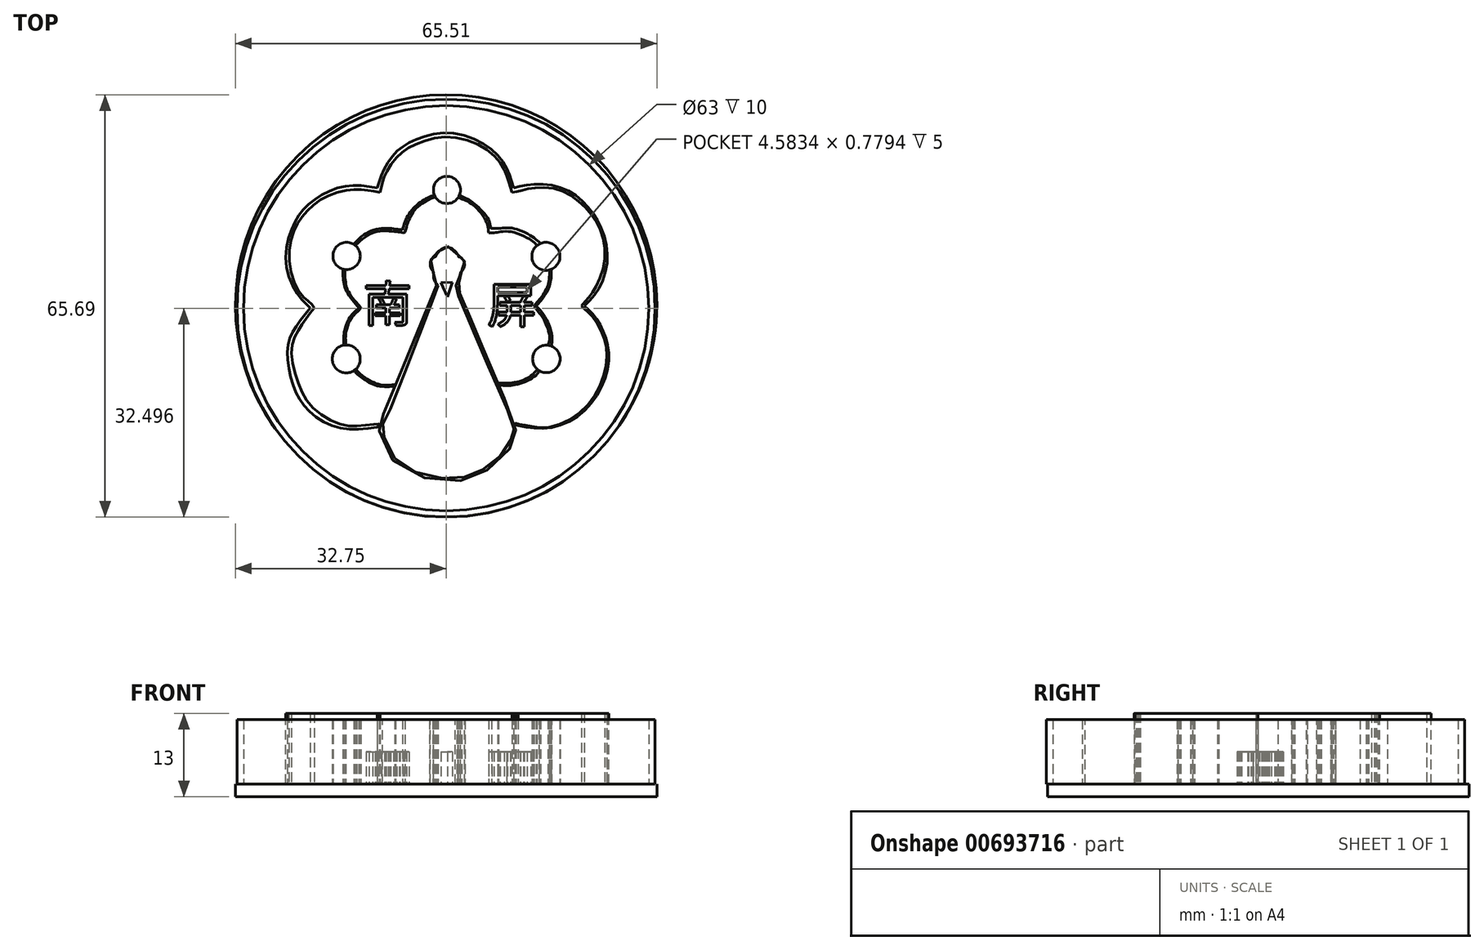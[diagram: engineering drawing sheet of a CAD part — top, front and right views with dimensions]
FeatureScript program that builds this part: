
annotation { "Feature Type Name" : "Feature", "Feature Type Description" : "" }
export const myFeature = defineFeature(function(context is Context, id is Id, definition is map)
    precondition{}
    {
        {
            var Q0;
            Q0=qCreatedBy(makeId("Top.planeOp"),FACE);
            var sketch = newSketch(context, id + "F0", { "sketchPlane" : qUnion([Q0])});
            skCircle(sketch, "E0", {"center": v(0, -1.24) * mm, "radius": 32.5 * mm});
            skCircle(sketch, "E1", {"center": v(0, -1.24) * mm, "radius": 31.5 * mm});
            skSolve(sketch);
        }
        {
            var Q0;
            Q0 = qSketchRegion(id + "F0", true);
            extrude(context, id + "F1", {"entities" : qUnion([Q0]), "depth" : 10 * mm, "offsetDistance" : 25 * mm});
        }
        {
            var Q0;
            Q0=qCreatedBy(makeId("Top.planeOp"),FACE);
            var sketch = newSketch(context, id + "F2", { "sketchPlane" : qUnion([Q0])});
            skCircle(sketch, "E2", {"center": v(15.51, 6.81) * mm, "radius": 2.18 * mm});
            skCircle(sketch, "E3", {"center": v(15.58, -9.13) * mm, "radius": 2.14 * mm});
            skCircle(sketch, "E4", {"center": v(-15.52, -9.14) * mm, "radius": 2.18 * mm});
            skCircle(sketch, "E5", {"center": v(-15.47, 6.87) * mm, "radius": 2.12 * mm});
            skCircle(sketch, "E6", {"center": v(0.13, 17.14) * mm, "radius": 2.1 * mm});
            skSolve(sketch);
        }
        {
            var Q0;
            Q0 = qSketchRegion(id + "F2", true);
            extrude(context, id + "F3", {"entities" : qUnion([Q0]), "depth" : 10 * mm, "offsetDistance" : 25 * mm});
        }
        {
            var Q0;
            Q0=qCreatedBy(makeId("Top.planeOp"),FACE);
            var sketch = newSketch(context, id + "F4", { "sketchPlane" : qUnion([Q0])});
            skFitSpline(sketch, "E7", {"points": [v(-21.1, -1.21) * mm, v(-22.88, 0.65) * mm, v(-24.9, 5.56) * mm, v(-23.94, 11.21) * mm, v(-22.06, 14.24) * mm, v(-18.83, 16.65) * mm, v(-14.76, 17.84) * mm, v(-10.69, 17.46) * mm], "startDerivative": vector(-15.64, 13.84) * mm, "endDerivative": vector(28.64, -5.04) * mm});
            skFitSpline(sketch, "E8", {"points": [v(-10.69, 17.46) * mm, v(-9.79, 20.1) * mm, v(-7.74, 23.04) * mm, v(-4.88, 24.89) * mm, v(0.49, 26.01) * mm, v(6.8, 23.66) * mm, v(9.52, 20.32) * mm, v(10.5, 17.46) * mm], "startDerivative": vector(5.97, 21.97) * mm, "endDerivative": vector(6.22, -23.18) * mm});
            skFitSpline(sketch, "E9", {"points": [v(10.5, 17.46) * mm, v(13.42, 18.02) * mm, v(18, 17.46) * mm, v(21.7, 14.88) * mm, v(24.05, 11.4) * mm, v(25.07, 6.52) * mm, v(23.76, 1.87) * mm, v(21.5, -0.88) * mm], "startDerivative": vector(22.64, 5.92) * mm, "endDerivative": vector(-18.53, -18.75) * mm});
            skFitSpline(sketch, "E10", {"points": [v(21.5, -0.88) * mm, v(23.02, -2.42) * mm, v(24.53, -5.1) * mm, v(25.3, -8.5) * mm, v(24.21, -13.35) * mm, v(20.62, -17.91) * mm, v(15.57, -19.91) * mm, v(11.2, -19.5) * mm], "startDerivative": vector(15.05, -13.26) * mm, "endDerivative": vector(-28.75, 5.7) * mm});
            skFitSpline(sketch, "E11", {"points": [v(-21.1, -1.21) * mm, v(-23.65, -4.6) * mm, v(-24.66, -7.87) * mm, v(-23.85, -12.93) * mm, v(-21.72, -16.82) * mm, v(-16.96, -19.78) * mm, v(-10.69, -19.78) * mm], "startDerivative": vector(-18.06, -21.75) * mm, "endDerivative": vector(33.82, 4.07) * mm});
            skFitSpline(sketch, "E12", {"points": [v(-10.69, -19.78) * mm, v(-10.52, -19.78) * mm, v(-10.39, -19.27) * mm, v(-10.5, -19.22) * mm, v(-12.99, -19.5) * mm, v(-16.5, -19.27) * mm, v(-20.9, -16.53) * mm, v(-23.06, -12.64) * mm, v(-24.05, -7.85) * mm, v(-23.13, -4.96) * mm, v(-21.74, -2.85) * mm, v(-20.5, -1.21) * mm], "startDerivative": vector(6.87, -2.87) * mm, "endDerivative": vector(13.9, 18.09) * mm});
            skFitSpline(sketch, "E13", {"points": [v(-20.5, -1.21) * mm, v(-21.1, -0.42) * mm, v(-22.5, 0.83) * mm, v(-24.36, 5.7) * mm, v(-23.6, 10.88) * mm, v(-21.7, 13.76) * mm, v(-18.68, 16.06) * mm, v(-14.7, 17.18) * mm, v(-12.24, 17.1) * mm, v(-10.28, 16.76) * mm], "startDerivative": vector(-8, 12.9) * mm, "endDerivative": vector(21.6, -4.05) * mm});
            skFitSpline(sketch, "E14", {"points": [v(-10.28, 16.76) * mm, v(-9.96, 18.1) * mm, v(-9.35, 19.75) * mm, v(-7.43, 22.48) * mm, v(-4.73, 24.25) * mm, v(0.43, 25.39) * mm, v(6.35, 23.4) * mm, v(9.03, 20.32) * mm, v(9.75, 18.32) * mm, v(10.22, 16.76) * mm], "startDerivative": vector(4.05, 17.8) * mm, "endDerivative": vector(5.84, -18.76) * mm});
            skFitSpline(sketch, "E15", {"points": [v(10.22, 16.76) * mm, v(11.53, 17.03) * mm, v(13.59, 17.46) * mm, v(17.82, 17.1) * mm, v(21.5, 14.55) * mm, v(23.76, 11.38) * mm, v(24.66, 6.7) * mm, v(23.34, 2.15) * mm, v(22.05, 0.32) * mm, v(21.06, -0.88) * mm], "startDerivative": vector(17.5, 3.26) * mm, "endDerivative": vector(-12.22, -15.06) * mm});
            skFitSpline(sketch, "E16", {"points": [v(21.06, -0.88) * mm, v(21.72, -1.57) * mm, v(22.75, -2.52) * mm, v(24.3, -5.23) * mm, v(25, -8.52) * mm, v(24, -13.1) * mm, v(20.64, -17.6) * mm, v(15.57, -19.78) * mm, v(12.62, -19.51) * mm, v(11.2, -19.26) * mm, v(10.7, -19.16) * mm, v(10.82, -19.44) * mm], "startDerivative": vector(10.7, -12.03) * mm, "endDerivative": vector(6.4, -11.24) * mm});
            skFitSpline(sketch, "E17", {"points": [v(10.82, -19.44) * mm, v(11.2, -19.5) * mm], "startDerivative": vector(0.4, -0.06) * mm, "endDerivative": vector(0.4, -0.06) * mm});
            skSolve(sketch);
        }
        {
            var Q0;
            Q0 = qSketchRegion(id + "F4", true);
            extrude(context, id + "F5", {"entities" : qUnion([Q0]), "depth" : 5 * mm, "offsetDistance" : 25 * mm});
        }
        {
            var Q0;
            Q0=qCreatedBy(makeId("Top.planeOp"),FACE);
            var sketch = newSketch(context, id + "F6", { "sketchPlane" : qUnion([Q0])});
            skSolve(sketch);
        }
        {
            var Q0;
            Q0=qCreatedBy(makeId("Top.planeOp"),FACE);
            var sketch = newSketch(context, id + "F7", { "sketchPlane" : qUnion([Q0])});
            skCircle(sketch, "E18", {"center": v(0, -0.8) * mm, "radius": 32.75 * mm});
            skPoint(sketch, "E18.first.point", {"position": v(31.84, -8.48) * mm});
            skPoint(sketch, "E18.second.point", {"position": v(-32.05, 5.96) * mm});
            skPoint(sketch, "E18.third.point", {"position": v(-26.8, -19.64) * mm});
            skSolve(sketch);
        }
        {
            var Q0;
            Q0 = qSketchRegion(id + "F7", true);
            extrude(context, id + "F8", {"entities" : qUnion([Q0]), "oppositeDirection" : true, "depth" : 2 * mm, "offsetDistance" : 25 * mm});
        }
        {
            var Q0;
            Q0 = qSketchRegion(id + "F6", true);
            var Q1;
            Q1=makeQuery(id+"F5.opExtrude","CAP_FACE",FACE,{"disambiguationData":[OSD([sQuery(id+"F4.wireOp",EDGE,"E7"),sQuery(id+"F4.wireOp",EDGE,"E8"),sQuery(id+"F4.wireOp",EDGE,"E9"),sQuery(id+"F4.wireOp",EDGE,"E10"),sQuery(id+"F4.wireOp",EDGE,"E11"),sQuery(id+"F4.wireOp",EDGE,"E12"),sQuery(id+"F4.wireOp",EDGE,"E13"),sQuery(id+"F4.wireOp",EDGE,"E14"),sQuery(id+"F4.wireOp",EDGE,"E15"),sQuery(id+"F4.wireOp",EDGE,"E16"),sQuery(id+"F4.wireOp",EDGE,"E17")])],"isStart":false});
            extrude(context, id + "F9", {"entities" : qUnion([Q0, Q1]), "operationType" : NewBodyOperationType.ADD, "depth" : 6 * mm, "offsetDistance" : 25 * mm});
        }
        {
            var Q0;
            Q0=qCreatedBy(makeId("Top.planeOp"),FACE);
            var sketch = newSketch(context, id + "F10", { "sketchPlane" : qUnion([Q0])});
            skFitSpline(sketch, "E19", {"points": [v(-1.5, 2.26) * mm, v(-2.02, 3.37) * mm, v(-2, 4.39) * mm, v(-2.02, 4.38) * mm, v(-2.45, 5.02) * mm, v(-2.53, 5.85) * mm, v(-2.3, 6.4) * mm, v(-1.75, 6.8) * mm, v(-1.71, 6.8) * mm, v(-1.58, 7.1) * mm, v(-0.85, 7.94) * mm, v(-0.37, 8.25) * mm, v(0.05, 8.36) * mm, v(0.5, 8.31) * mm, v(1.26, 7.92) * mm, v(1.9, 7.1) * mm, v(1.97, 6.81) * mm, v(1.97, 6.79) * mm, v(2.07, 6.8) * mm, v(2.47, 6.61) * mm, v(2.84, 6.07) * mm, v(2.94, 5.37) * mm, v(2.66, 4.61) * mm, v(2.4, 4.4) * mm, v(2.35, 4.38) * mm, v(2.4, 4.3) * mm, v(2.28, 3.57) * mm, v(2.07, 2.85) * mm, v(1.76, 2.2) * mm, v(1.7, 2.1) * mm, v(1.7, 2.08) * mm, v(1.92, 1.53) * mm, v(3.06, -1.03) * mm, v(4.18, -3.76) * mm, v(7.4, -11.4) * mm, v(10.83, -19.9) * mm, v(10.8, -20.4) * mm, v(10.5, -21.78) * mm, v(8.69, -24.67) * mm, v(5, -27.13) * mm, v(1.71, -28.1) * mm, v(-4.27, -27.38) * mm, v(-8.87, -24.14) * mm, v(-10.4, -20.11) * mm, v(-10.3, -19.12) * mm, v(-9.65, -17.5) * mm, v(-3.8, -3.3) * mm, v(-1.57, 1.92) * mm, v(-1.5, 2.26) * mm]});
            skFitSpline(sketch, "E20", {"points": [v(-1.25, 2.25) * mm, v(-1.39, 1.81) * mm, v(-3.47, -3.55) * mm, v(-9.04, -17.75) * mm, v(-9.8, -19.26) * mm, v(-9.88, -20.11) * mm, v(-8.6, -23.75) * mm, v(-4.24, -26.95) * mm, v(1.7, -27.72) * mm, v(4.78, -26.84) * mm, v(8.23, -24.49) * mm, v(10.09, -21.67) * mm, v(10.47, -20.33) * mm, v(10.53, -19.9) * mm, v(8.7, -15.16) * mm, v(7.1, -11.5) * mm, v(3.84, -3.85) * mm, v(2.71, -1.2) * mm, v(1.44, 2.02) * mm, v(1.46, 2.1) * mm, v(1.57, 2.35) * mm, v(1.92, 3.04) * mm, v(2.11, 3.7) * mm, v(2.26, 4.21) * mm, v(2.24, 4.28) * mm, v(2.23, 4.34) * mm, v(2.28, 4.38) * mm], "startDerivative": vector(-5.5, -19.67) * mm, "endDerivative": vector(9.01, 2.13) * mm});
            skFitSpline(sketch, "E21", {"points": [v(2.28, 4.38) * mm, v(2.3, 4.42) * mm, v(2.48, 4.5) * mm, v(2.58, 4.65) * mm, v(2.72, 4.89) * mm, v(2.88, 5.37) * mm, v(2.78, 6.05) * mm, v(2.45, 6.56) * mm, v(2.09, 6.73) * mm, v(1.94, 6.7) * mm, v(1.92, 6.71) * mm, v(1.9, 6.7) * mm, v(1.91, 6.81) * mm, v(1.85, 7.06) * mm, v(1.2, 7.85) * mm, v(0.48, 8.23) * mm, v(0.07, 8.27) * mm, v(-0.34, 8.16) * mm, v(-0.77, 7.9) * mm, v(-1.5, 7.07) * mm, v(-1.66, 6.76) * mm, v(-1.67, 6.75) * mm, v(-1.74, 6.74) * mm, v(-2.26, 6.37) * mm, v(-2.46, 5.84) * mm, v(-2.48, 5.38) * mm, v(-2.4, 5.06) * mm, v(-2.08, 4.5) * mm, v(-1.97, 4.43) * mm, v(-1.97, 4.44) * mm, v(-1.96, 4.24) * mm, v(-1.95, 3.57) * mm, v(-1.81, 3.02) * mm, v(-1.25, 2.25) * mm], "startDerivative": vector(0.63, 3.84) * mm, "endDerivative": vector(12.96, -15.51) * mm});
            skSolve(sketch);
        }
        {
            var Q0;
            Q0 = qSketchRegion(id + "F10", true);
            extrude(context, id + "F11", {"entities" : qUnion([Q0]), "operationType" : NewBodyOperationType.ADD, "depth" : 10 * mm, "offsetDistance" : 25 * mm});
        }
        {
            var Q0;
            Q0=qCreatedBy(makeId("Top.planeOp"),FACE);
            var sketch = newSketch(context, id + "F12", { "sketchPlane" : qUnion([Q0])});
            skFitSpline(sketch, "E22", {"points": [v(-1.83, 16.35) * mm, v(-3.1, 15.82) * mm, v(-4.84, 14.55) * mm, v(-6.14, 12.76) * mm, v(-6.8, 10.9) * mm], "startDerivative": vector(-5.76, -2.1) * mm, "endDerivative": vector(-2.16, -7.38) * mm});
            skFitSpline(sketch, "E23", {"points": [v(-6.8, 10.9) * mm, v(-7.69, 11.05) * mm, v(-9.21, 11.2) * mm, v(-11.34, 10.9) * mm, v(-13.43, 9.67) * mm, v(-14.32, 8.7) * mm], "startDerivative": vector(-5.58, 0.95) * mm, "endDerivative": vector(-4.17, -5.18) * mm});
            skFitSpline(sketch, "E24", {"points": [v(-14.32, 8.7) * mm, v(-14.14, 8.57) * mm], "startDerivative": vector(0.18, -0.14) * mm, "endDerivative": vector(0.18, -0.14) * mm});
            skFitSpline(sketch, "E25", {"points": [v(-14.14, 8.57) * mm, v(-13.93, 8.7) * mm, v(-13.22, 9.35) * mm, v(-11.23, 10.55) * mm, v(-9.18, 10.77) * mm, v(-7.72, 10.66) * mm, v(-7.08, 10.55) * mm, v(-6.55, 10.48) * mm, v(-6.37, 10.62) * mm], "startDerivative": vector(2.96, 1.72) * mm, "endDerivative": vector(2.27, 2.91) * mm});
            skFitSpline(sketch, "E26", {"points": [v(-6.37, 10.62) * mm, v(-5.7, 12.63) * mm, v(-4.63, 14.3) * mm, v(-2.92, 15.52) * mm, v(-2.14, 15.9) * mm, v(-1.7, 16.07) * mm], "startDerivative": vector(2.46, 8.41) * mm, "endDerivative": vector(3.68, 1.34) * mm});
            skFitSpline(sketch, "E27", {"points": [v(-1.7, 16.07) * mm, v(-1.83, 16.35) * mm], "startDerivative": vector(-0.13, 0.28) * mm, "endDerivative": vector(-0.13, 0.28) * mm});
            skFitSpline(sketch, "E28", {"points": [v(-15.98, 4.82) * mm, v(-16.04, 4.32) * mm, v(-15.9, 2.65) * mm, v(-15.24, 0.96) * mm, v(-13.69, -1.04) * mm, v(-13.57, -1.2) * mm, v(-13.57, -1.17) * mm], "startDerivative": vector(-0.58, -3.26) * mm, "endDerivative": vector(-0.13, 1.48) * mm});
            skFitSpline(sketch, "E29", {"points": [v(-13.57, -1.2) * mm, v(-14.25, -1.8) * mm, v(-15.1, -2.9) * mm, v(-15.88, -5.28) * mm, v(-15.88, -6.97) * mm], "startDerivative": vector(-3.52, -3) * mm, "endDerivative": vector(0.54, -6.05) * mm});
            skFitSpline(sketch, "E30", {"points": [v(-15.88, -6.97) * mm, v(-15.87, -7) * mm], "startDerivative": vector(0, -0.03) * mm, "endDerivative": vector(0, -0.03) * mm});
            skFitSpline(sketch, "E31", {"points": [v(-15.87, -7) * mm, v(-15.6, -6.97) * mm], "startDerivative": vector(0.27, 0.03) * mm, "endDerivative": vector(0.27, 0.03) * mm});
            skFitSpline(sketch, "E32", {"points": [v(-15.6, -6.97) * mm, v(-15.6, -6.48) * mm, v(-15.6, -5.4) * mm, v(-14.85, -3) * mm, v(-14, -1.99) * mm, v(-13.57, -1.58) * mm, v(-13.25, -1.2) * mm, v(-13.22, -1.2) * mm], "startDerivative": vector(0.1, 4) * mm, "endDerivative": vector(0.71, -0.32) * mm});
            skFitSpline(sketch, "E33", {"points": [v(-13.22, -1.2) * mm, v(-13.4, -1) * mm, v(-15, 0.99) * mm, v(-15.6, 2.65) * mm, v(-15.73, 4.3) * mm, v(-15.68, 4.76) * mm], "startDerivative": vector(-1.15, 1.57) * mm, "endDerivative": vector(0.61, 3.02) * mm});
            skFitSpline(sketch, "E34", {"points": [v(-15.98, 4.82) * mm, v(-15.68, 4.76) * mm], "startDerivative": vector(0.3, -0.06) * mm, "endDerivative": vector(0.3, -0.06) * mm});
            skFitSpline(sketch, "E35", {"points": [v(-14.26, -10.9) * mm, v(-12.72, -12.4) * mm, v(-10.42, -13.4) * mm, v(-8, -13.46) * mm], "startDerivative": vector(4.4, -4.96) * mm, "endDerivative": vector(7.17, 0.46) * mm});
            skFitSpline(sketch, "E36", {"points": [v(-8, -13.46) * mm, v(-7.85, -13.1) * mm, v(-7.88, -13.1) * mm], "startDerivative": vector(0.32, 0.65) * mm, "endDerivative": vector(-0.19, -0.08) * mm});
            skFitSpline(sketch, "E37", {"points": [v(-7.87, -13.1) * mm, v(-8.75, -13.1) * mm, v(-10.32, -13.02) * mm, v(-12.44, -12.16) * mm, v(-13.5, -11.33) * mm, v(-14.03, -10.72) * mm], "startDerivative": vector(-5.06, 0.07) * mm, "endDerivative": vector(-3.17, 3.86) * mm});
            skFitSpline(sketch, "E38", {"points": [v(-14.03, -10.72) * mm, v(-14.26, -10.9) * mm], "startDerivative": vector(-0.23, -0.18) * mm, "endDerivative": vector(-0.23, -0.18) * mm});
            skFitSpline(sketch, "E39", {"points": [v(8.18, -13.17) * mm, v(8.75, -13.23) * mm, v(9.97, -13.25) * mm, v(12.33, -12.67) * mm, v(14.3, -11.33) * mm, v(14.5, -10.98) * mm, v(14.5, -11) * mm], "startDerivative": vector(3.96, -0.53) * mm, "endDerivative": vector(-0.08, -0.8) * mm});
            skFitSpline(sketch, "E40", {"points": [v(14.51, -10.99) * mm, v(14.14, -10.72) * mm], "startDerivative": vector(-0.37, 0.27) * mm, "endDerivative": vector(-0.37, 0.27) * mm});
            skFitSpline(sketch, "E41", {"points": [v(14.14, -10.72) * mm, v(13.93, -11.08) * mm, v(12.29, -12.3) * mm, v(10, -12.87) * mm, v(8.75, -12.92) * mm, v(8.05, -12.87) * mm], "startDerivative": vector(-1.14, -2.73) * mm, "endDerivative": vector(-4.4, 0.35) * mm});
            skFitSpline(sketch, "E42", {"points": [v(8.05, -12.87) * mm, v(8.18, -13.17) * mm], "startDerivative": vector(0.13, -0.3) * mm, "endDerivative": vector(0.13, -0.3) * mm});
            skFitSpline(sketch, "E43", {"points": [v(2.04, 16.35) * mm, v(3.2, 15.82) * mm, v(4.82, 14.64) * mm, v(6.68, 12.32) * mm, v(6.99, 11.2) * mm, v(7.06, 11.2) * mm], "startDerivative": vector(5.68, -2.36) * mm, "endDerivative": vector(1.66, 0.6) * mm});
            skFitSpline(sketch, "E44", {"points": [v(7.06, 11.2) * mm, v(8.35, 11.2) * mm, v(10.34, 11.2) * mm, v(13.15, 10.04) * mm, v(14.67, 8.85) * mm], "startDerivative": vector(6.18, -0.2) * mm, "endDerivative": vector(5.46, -4.87) * mm});
            skFitSpline(sketch, "E45", {"points": [v(14.67, 8.85) * mm, v(14.14, 8.5) * mm], "startDerivative": vector(-0.52, -0.35) * mm, "endDerivative": vector(-0.52, -0.35) * mm});
            skFitSpline(sketch, "E46", {"points": [v(14.14, 8.5) * mm, v(13.81, 8.85) * mm, v(12.96, 9.5) * mm, v(10.2, 10.62) * mm, v(8.35, 10.62) * mm, v(7.5, 10.49) * mm, v(6.61, 10.49) * mm], "startDerivative": vector(-2.93, 3.27) * mm, "endDerivative": vector(-6.47, 0.26) * mm});
            skFitSpline(sketch, "E47", {"points": [v(6.61, 10.49) * mm, v(6.3, 12.08) * mm, v(4.7, 14.35) * mm, v(3.14, 15.45) * mm, v(2.25, 15.82) * mm, v(1.9, 15.96) * mm], "startDerivative": vector(-0.58, 7.07) * mm, "endDerivative": vector(-3.02, 1.32) * mm});
            skFitSpline(sketch, "E48", {"points": [v(1.9, 15.96) * mm, v(2.04, 16.35) * mm], "startDerivative": vector(0.14, 0.4) * mm, "endDerivative": vector(0.14, 0.4) * mm});
            skFitSpline(sketch, "E49", {"points": [v(16.3, 4.76) * mm, v(16.34, 4.4) * mm, v(16.27, 3.1) * mm, v(15.83, 1.6) * mm, v(14.94, 0.19) * mm, v(14, -0.93) * mm], "startDerivative": vector(0.42, -2.76) * mm, "endDerivative": vector(-4.24, -4.87) * mm});
            skFitSpline(sketch, "E50", {"points": [v(14, -0.93) * mm, v(14.3, -1.2) * mm, v(15.02, -2.06) * mm, v(15.45, -2.7) * mm, v(16.04, -3.98) * mm, v(16.48, -5.75) * mm, v(16.34, -7.13) * mm], "startDerivative": vector(2.54, -2.2) * mm, "endDerivative": vector(-1.38, -7.07) * mm});
            skFitSpline(sketch, "E51", {"points": [v(16.34, -7.13) * mm, v(15.82, -7) * mm], "startDerivative": vector(-0.52, 0.14) * mm, "endDerivative": vector(-0.52, 0.14) * mm});
            skFitSpline(sketch, "E52", {"points": [v(15.82, -7) * mm, v(16, -6.6) * mm, v(16.11, -5.78) * mm, v(15.67, -4.1) * mm, v(15.13, -2.9) * mm, v(14.8, -2.39) * mm, v(14, -1.4) * mm, v(13.65, -1) * mm], "startDerivative": vector(1.84, 3.7) * mm, "endDerivative": vector(-2.8, 3.1) * mm});
            skFitSpline(sketch, "E53", {"points": [v(13.65, -1) * mm, v(14, -0.46) * mm, v(14.67, 0.33) * mm, v(15.56, 1.7) * mm, v(16, 3.1) * mm, v(16.1, 4.43) * mm, v(16.1, 4.65) * mm], "startDerivative": vector(2.42, 3.87) * mm, "endDerivative": vector(-0.05, 2.13) * mm});
            skFitSpline(sketch, "E54", {"points": [v(16.1, 4.65) * mm, v(16.1, 4.71) * mm], "startDerivative": vector(0, 0.06) * mm, "endDerivative": vector(0, 0.06) * mm});
            skFitSpline(sketch, "E55", {"points": [v(16.1, 4.71) * mm, v(16.3, 4.76) * mm], "startDerivative": vector(0.2, 0.05) * mm, "endDerivative": vector(0.2, 0.05) * mm});
            skSolve(sketch);
        }
        {
            var Q0;
            Q0 = qSketchRegion(id + "F12", true);
            extrude(context, id + "F13", {"entities" : qUnion([Q0]), "depth" : 10 * mm, "offsetDistance" : 25 * mm});
        }
        {
            var Q0;
            Q0=qCreatedBy(makeId("Top.planeOp"),FACE);
            var sketch = newSketch(context, id + "F14", { "sketchPlane" : qUnion([Q0])});
            skFitSpline(sketch, "E56", {"points": [v(-14.25, -10.87) * mm, v(-14, -11.34) * mm, v(-12.85, -12.24) * mm, v(-10.94, -13.25) * mm, v(-7.99, -13.42) * mm], "startDerivative": vector(1.17, -3.2) * mm, "endDerivative": vector(9.35, 0.35) * mm});
            skFitSpline(sketch, "E57", {"points": [v(-7.99, -13.42) * mm, v(-7.85, -13.12) * mm], "startDerivative": vector(0.14, 0.3) * mm, "endDerivative": vector(0.14, 0.3) * mm});
            skFitSpline(sketch, "E58", {"points": [v(-14.25, -10.87) * mm, v(-14, -10.68) * mm], "startDerivative": vector(0.25, 0.2) * mm, "endDerivative": vector(0.25, 0.2) * mm});
            skFitSpline(sketch, "E59", {"points": [v(-14, -10.68) * mm, v(-13.9, -10.87) * mm], "startDerivative": vector(0.1, -0.2) * mm, "endDerivative": vector(0.1, -0.2) * mm});
            skFitSpline(sketch, "E60", {"points": [v(-13.9, -10.87) * mm, v(-13.35, -11.47) * mm, v(-12.8, -11.91) * mm, v(-10.97, -12.92) * mm, v(-9.02, -13.22) * mm, v(-7.85, -13.12) * mm], "startDerivative": vector(3.54, -4.1) * mm, "endDerivative": vector(5.76, 0.8) * mm});
            skSolve(sketch);
        }
        {
            var Q0;
            Q0 = qSketchRegion(id + "F14", true);
            extrude(context, id + "F15", {"entities" : qUnion([Q0]), "depth" : 10 * mm, "offsetDistance" : 25 * mm});
        }
        {
            var Q0;
            Q0=qCreatedBy(makeId("Top.planeOp"),FACE);
            var sketch = newSketch(context, id + "F16", { "sketchPlane" : qUnion([Q0])});
            skText(sketch, "E61", { "text": "南", "fontName": "NotoSansCJKtc-Regular.otf"});
            skText(sketch, "E62", { "text": "屏", "fontName": "NotoSansCJKtc-Regular.otf"});
            const initialGuessF16  = {"E61": [-0.0129, -0.00335, 1, 0, 0.0055], "E62": [0.00638, -0.00353, 1, 0, 0.0055]};
            skSetInitialGuess(sketch, initialGuessF16);
            skSolve(sketch);
        }
        {
            var Q0;
            Q0 = qSketchRegion(id + "F16", true);
            extrude(context, id + "F17", {"entities" : qUnion([Q0]), "operationType" : NewBodyOperationType.ADD, "depth" : 5 * mm, "offsetDistance" : 25 * mm});
        }
        {
            var Q0;
            Q0=qCreatedBy(makeId("Top.planeOp"),FACE);
            var sketch = newSketch(context, id + "F18", { "sketchPlane" : qUnion([Q0])});
            skFitSpline(sketch, "E63", {"points": [v(-0.8, 2.74) * mm, v(0.95, 2.77) * mm], "startDerivative": vector(1.74, 0.03) * mm, "endDerivative": vector(1.74, 0.03) * mm});
            skFitSpline(sketch, "E64", {"points": [v(0.95, 2.77) * mm, v(0.2, 0.5) * mm], "startDerivative": vector(-0.75, -2.27) * mm, "endDerivative": vector(-0.75, -2.27) * mm});
            skFitSpline(sketch, "E65", {"points": [v(-0.8, 2.74) * mm, v(0.2, 0.5) * mm], "startDerivative": vector(1, -2.24) * mm, "endDerivative": vector(1, -2.24) * mm});
            skSolve(sketch);
        }
        {
            var Q0;
            Q0 = qSketchRegion(id + "F18", true);
            extrude(context, id + "F19", {"entities" : qUnion([Q0]), "operationType" : NewBodyOperationType.ADD, "depth" : 5 * mm, "offsetDistance" : 25 * mm});
        }
    });
